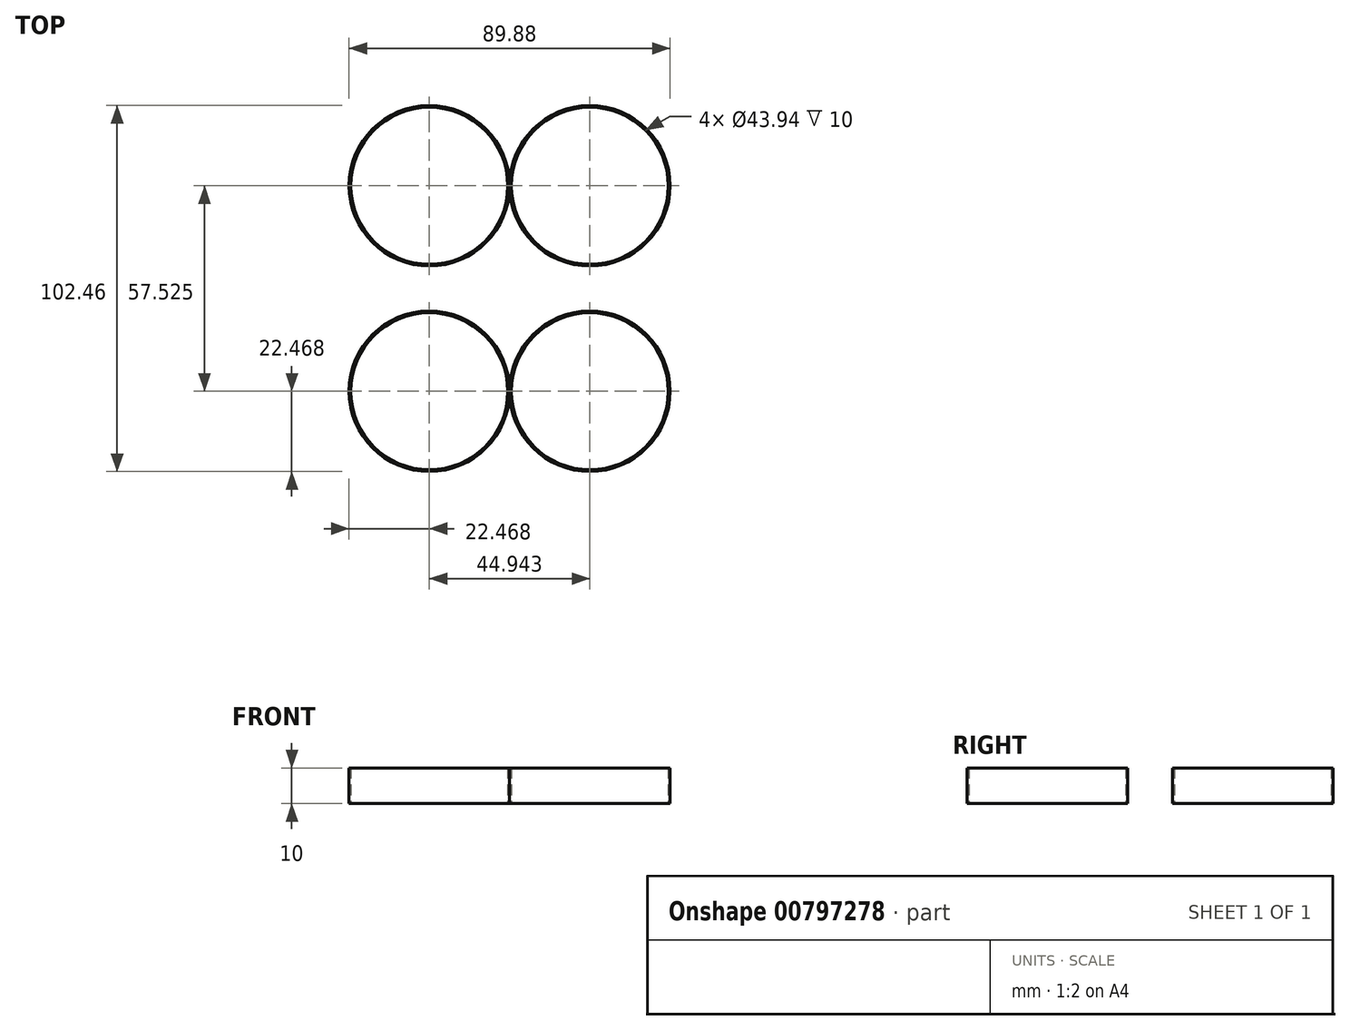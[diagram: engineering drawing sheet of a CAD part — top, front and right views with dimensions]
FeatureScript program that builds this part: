
annotation { "Feature Type Name" : "Feature", "Feature Type Description" : "" }
export const myFeature = defineFeature(function(context is Context, id is Id, definition is map)
    precondition{}
    {
        {
            var Q0;
            Q0=qCreatedBy(makeId("Top.planeOp"),FACE);
            var sketch = newSketch(context, id + "F0", { "sketchPlane" : qUnion([Q0])});
            skLineSegment(sketch, "E0.bottom", {"start": v(8, -8) * mm, "end": v(-8, -8) * mm, "construction": true});
            skLineSegment(sketch, "E0.top", {"start": v(8, 8) * mm, "end": v(-8, 8) * mm, "construction": true});
            skLineSegment(sketch, "E0.left", {"start": v(8, -8) * mm, "end": v(8, 8) * mm, "construction": true});
            skLineSegment(sketch, "E0.right", {"start": v(-8, -8) * mm, "end": v(-8, 8) * mm, "construction": true});
            skPoint(sketch, "E0.middle", {"position": v(0, 0) * mm});
            skCircle(sketch, "E1", {"center": v(0, 0) * mm, "radius": 36.5 * mm, "construction": true});
            skLineSegment(sketch, "E2", {"start": v(0, 0) * mm, "end": v(34.78, 44.52) * mm, "construction": true});
            skPoint(sketch, "E3", {"position": v(22.47, 28.76) * mm});
            skCircle(sketch, "E4", {"center": v(22.47, 28.76) * mm, "radius": 20 * mm, "construction": true});
            skLineSegment(sketch, "E5.bottom", {"start": v(10, -10) * mm, "end": v(-10, -10) * mm, "construction": true});
            skLineSegment(sketch, "E5.top", {"start": v(10, 10) * mm, "end": v(-10, 10) * mm, "construction": true});
            skLineSegment(sketch, "E5.left", {"start": v(10, -10) * mm, "end": v(10, 10) * mm, "construction": true});
            skLineSegment(sketch, "E5.right", {"start": v(-10, -10) * mm, "end": v(-10, 10) * mm, "construction": true});
            skPoint(sketch, "E6", {"position": v(24.16, 30.93) * mm});
            skCircle(sketch, "E7", {"center": v(24.16, 30.93) * mm, "radius": 0.8 * mm});
            skCircle(sketch, "E8.1.0", {"center": v(19.75, 29.15) * mm, "radius": 0.8 * mm});
            skCircle(sketch, "E8.2.0", {"center": v(23.5, 26.21) * mm, "radius": 0.8 * mm});
            skCircle(sketch, "E9", {"center": v(22.47, 28.76) * mm, "radius": 1.5 * mm});
            skCircle(sketch, "E10", {"center": v(8, 8) * mm, "radius": 1 * mm});
            skLineSegment(sketch, "E11", {"start": v(0, 0) * mm, "end": v(0, 56.53) * mm, "construction": true});
            skCircle(sketch, "E12", {"center": v(22.47, 28.76) * mm, "radius": 22.47 * mm});
            skCircle(sketch, "E13", {"center": v(22.47, 28.76) * mm, "radius": 5 * mm, "construction": true});
            skCircle(sketch, "E14.0", {"center": v(22.47, 28.76) * mm, "radius": 21.97 * mm});
            skSolve(sketch);
        }
        {
            var Q0;
            Q0=makeQuery(id+"F0.imprint","IMPRINT",FACE,{"disambiguationData":[TD([[makeQuery(id+"F0.imprint","IMPRINT",EDGE,{"derivedFrom":sQuery(id+"F0.wireOp",EDGE,"E12")}),1.0]])]});
            extrude(context, id + "F1", {"entities" : qUnion([Q0]), "depth" : 10 * mm, "offsetDistance" : 25 * mm});
        }
        {
            var Q0;
            Q0=makeQuery(id+"F1.opExtrude","SWEPT_BODY",BODY,{"disambiguationData":[OSD([sQuery(id+"F0.wireOp",EDGE,"E12"),sQuery(id+"F0.wireOp",EDGE,"E14.0")])]});
            var Q1;
            Q1=qCreatedBy(makeId("Right.planeOp"),FACE);
            mirror(context, id + "F2", {"operationType" : NewBodyOperationType.ADD, "entities" : qUnion([Q0]), "mirrorPlane" : qUnion([Q1])});
        }
        {
            var Q0;
            Q0=makeQuery(id+"F2.opPattern","COPY",BODY,{"derivedFrom":makeQuery(id+"F1.opExtrude","SWEPT_BODY",BODY,{"disambiguationData":[OSD([sQuery(id+"F0.wireOp",EDGE,"E12"),sQuery(id+"F0.wireOp",EDGE,"E14.0")])]}),"instanceName":"1"});
            var Q1;
            Q1=makeQuery(id+"F1.opExtrude","SWEPT_BODY",BODY,{"disambiguationData":[OSD([sQuery(id+"F0.wireOp",EDGE,"E12"),sQuery(id+"F0.wireOp",EDGE,"E14.0")])]});
            var Q2;
            Q2=qCreatedBy(makeId("Front.planeOp"),FACE);
            mirror(context, id + "F3", {"entities" : qUnion([Q0, Q1]), "mirrorPlane" : qUnion([Q2])});
        }
    });
